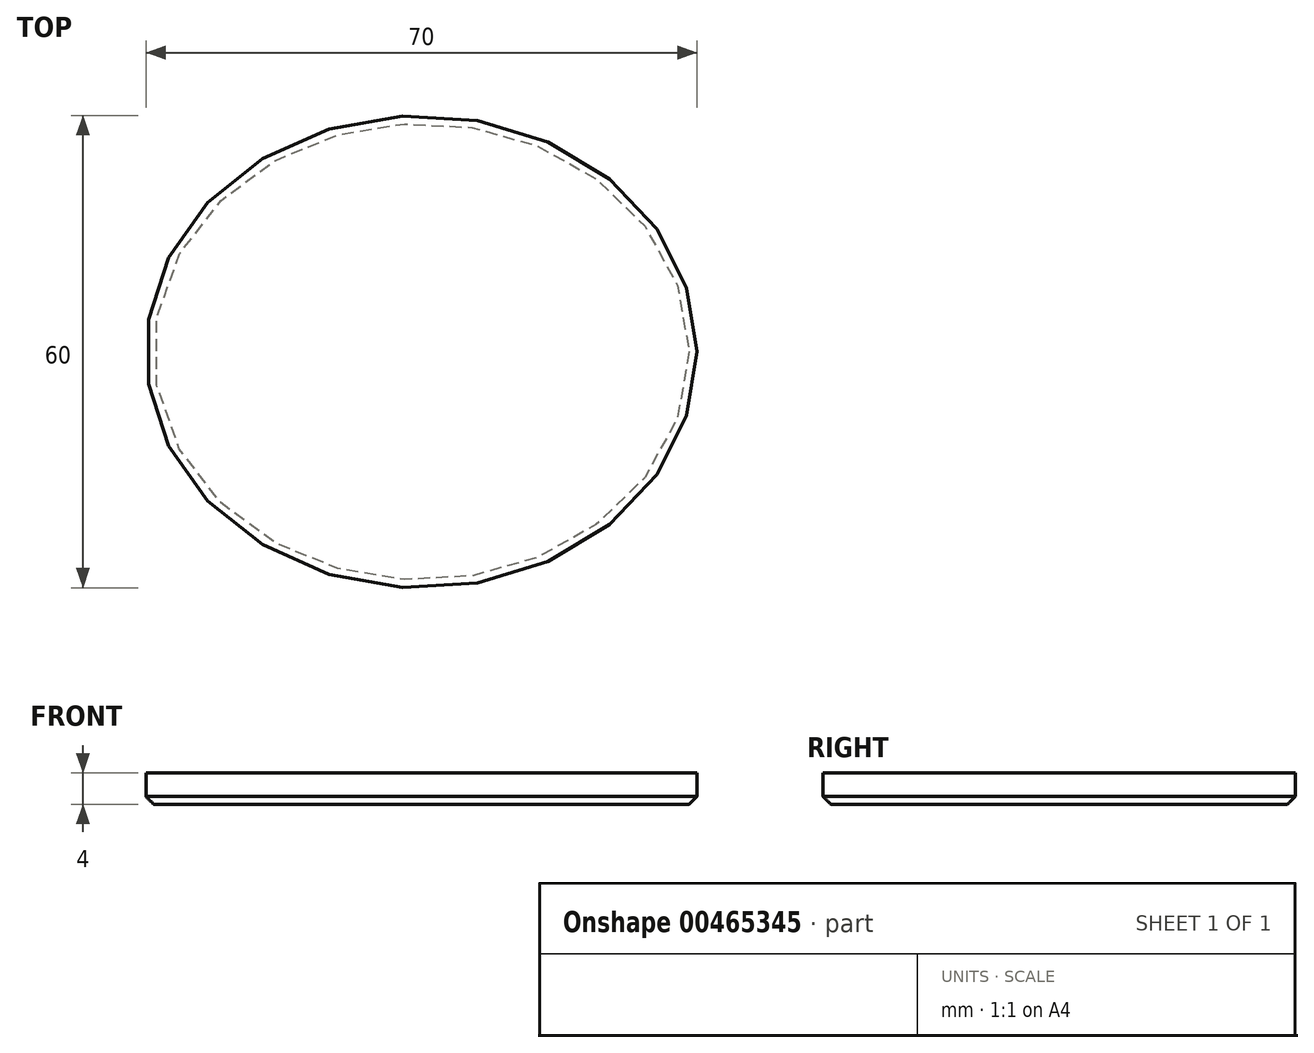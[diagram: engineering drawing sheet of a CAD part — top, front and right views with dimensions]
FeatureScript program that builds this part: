
annotation { "Feature Type Name" : "Feature", "Feature Type Description" : "" }
export const myFeature = defineFeature(function(context is Context, id is Id, definition is map)
    precondition{}
    {
        {
            var Q0;
            Q0=qCreatedBy(makeId("Top.planeOp"),FACE);
            var sketch = newSketch(context, id + "F0", { "sketchPlane" : qUnion([Q0])});
            skEllipse(sketch, "E0", {"center": v(0, 0) * mm, "majorRadius": 35 * mm, "minorRadius": 30 * mm, "majorAxis": v(1, 0)});
            skFitSpline(sketch, "E1.0", {"points": [v(31.97, -1.32) * mm, v(32.01, 0) * mm, v(31.97, 1.32) * mm, v(31.82, 3.06) * mm, v(31.45, 5.2) * mm, v(30.7, 7.73) * mm, v(29.68, 10.19) * mm, v(28.38, 12.56) * mm, v(26.8, 14.82) * mm, v(25.26, 16.6) * mm, v(23.9, 17.96) * mm, v(22.8, 18.94) * mm, v(21.66, 19.88) * mm, v(20.07, 21.05) * mm, v(17.96, 22.4) * mm, v(15.26, 23.78) * mm, v(12.41, 24.93) * mm, v(9.44, 25.84) * mm, v(6.37, 26.5) * mm, v(3.74, 26.84) * mm, v(1.61, 26.98) * mm, v(0, 27.01) * mm, v(-1.61, 26.98) * mm, v(-3.74, 26.84) * mm, v(-6.37, 26.5) * mm, v(-9.44, 25.84) * mm, v(-12.41, 24.93) * mm, v(-15.26, 23.78) * mm, v(-17.96, 22.4) * mm, v(-20.07, 21.05) * mm, v(-21.66, 19.88) * mm, v(-22.8, 18.94) * mm, v(-23.9, 17.96) * mm, v(-25.26, 16.6) * mm, v(-26.8, 14.82) * mm, v(-28.38, 12.56) * mm, v(-29.68, 10.19) * mm, v(-30.7, 7.73) * mm, v(-31.45, 5.2) * mm, v(-31.82, 3.06) * mm, v(-31.97, 1.32) * mm, v(-32.01, 0) * mm, v(-31.97, -1.32) * mm, v(-31.82, -3.06) * mm, v(-31.45, -5.2) * mm, v(-30.7, -7.73) * mm, v(-29.68, -10.19) * mm, v(-28.38, -12.56) * mm, v(-26.8, -14.82) * mm, v(-25.26, -16.6) * mm, v(-23.9, -17.96) * mm, v(-22.8, -18.94) * mm, v(-21.66, -19.88) * mm, v(-20.07, -21.05) * mm, v(-17.96, -22.4) * mm, v(-15.26, -23.78) * mm, v(-12.41, -24.93) * mm, v(-9.44, -25.84) * mm, v(-6.37, -26.5) * mm, v(-3.74, -26.84) * mm, v(-1.61, -26.98) * mm, v(0, -27.01) * mm, v(1.61, -26.98) * mm, v(3.74, -26.84) * mm, v(6.37, -26.5) * mm, v(9.44, -25.84) * mm, v(12.41, -24.93) * mm, v(15.26, -23.78) * mm, v(17.96, -22.4) * mm, v(20.07, -21.05) * mm, v(21.66, -19.88) * mm, v(22.8, -18.94) * mm, v(23.9, -17.96) * mm, v(25.26, -16.6) * mm, v(26.8, -14.82) * mm, v(28.38, -12.56) * mm, v(29.68, -10.19) * mm, v(30.7, -7.73) * mm, v(31.45, -5.2) * mm, v(31.82, -3.06) * mm, v(31.97, -1.32) * mm, v(32.01, 0) * mm, v(31.97, 1.32) * mm, v(31.97, -1.32) * mm]});
            skArc(sketch, "E2", {"start": v(-11.03, -2) * mm, "mid": v(-20.93, -3) * mm, "end": v(-11.03, -4) * mm});
            skArc(sketch, "E3.MirrorC", {"start": v(11.03, -2) * mm, "mid": v(20.93, -3) * mm, "end": v(11.03, -4) * mm});
            skLineSegment(sketch, "E4.0", {"start": v(-11.03, -4) * mm, "end": v(11.03, -4) * mm});
            skLineSegment(sketch, "E5.0", {"start": v(-11.03, -2) * mm, "end": v(11.03, -2) * mm});
            skPoint(sketch, "E6", {"position": v(0, -2) * mm});
            skSolve(sketch);
        }
        {
            var Q0;
            Q0=makeQuery(id+"F0.imprint","IMPRINT",FACE,{"disambiguationData":[TD([[makeQuery(id+"F0.imprint","IMPRINT",EDGE,{"derivedFrom":sQuery(id+"F0.wireOp",EDGE,"E0")}),1.0]])]});
            var Q1;
            Q1=makeQuery(id+"F0.imprint","IMPRINT",FACE,{"disambiguationData":[TD([[makeQuery(id+"F0.imprint","IMPRINT",EDGE,{"derivedFrom":sQuery(id+"F0.wireOp",EDGE,"E2")}),1.0]])]});
            extrude(context, id + "F1", {"entities" : qUnion([Q0, Q1]), "depth" : 4 * mm});
        }
        {
            var Q0;
            Q0=makeQuery(id+"F1.opExtrude","CAP_EDGE",EDGE,{"disambiguationData":[OSD([sQuery(id+"F0.wireOp",EDGE,"E0")])],"isStart":true});
            var Q1;
            Q1=makeQuery(id+"F1.opExtrude","CAP_EDGE",EDGE,{"disambiguationData":[OSD([sQuery(id+"F0.wireOp",EDGE,"E1.0")])],"isStart":true});
            var Q2;
            Q2=makeQuery(id+"F1.opExtrude","CAP_EDGE",EDGE,{"disambiguationData":[OSD([sQuery(id+"F0.wireOp",EDGE,"E3.MirrorC")])],"isStart":true});
            var Q3;
            Q3=makeQuery(id+"F1.opExtrude","CAP_EDGE",EDGE,{"disambiguationData":[OSD([sQuery(id+"F0.wireOp",EDGE,"E5.0")])],"isStart":true});
            var Q4;
            Q4=makeQuery(id+"F1.opExtrude","CAP_EDGE",EDGE,{"disambiguationData":[OSD([sQuery(id+"F0.wireOp",EDGE,"E2")])],"isStart":true});
            var Q5;
            Q5=makeQuery(id+"F1.opExtrude","CAP_EDGE",EDGE,{"disambiguationData":[OSD([sQuery(id+"F0.wireOp",EDGE,"E4.0")])],"isStart":true});
            chamfer(context, id + "F2", {"entities" : qUnion([Q0, Q1, Q2, Q3, Q4, Q5]), "width" : 1 * mm, "tangentPropagation" : true});
        }
    });
